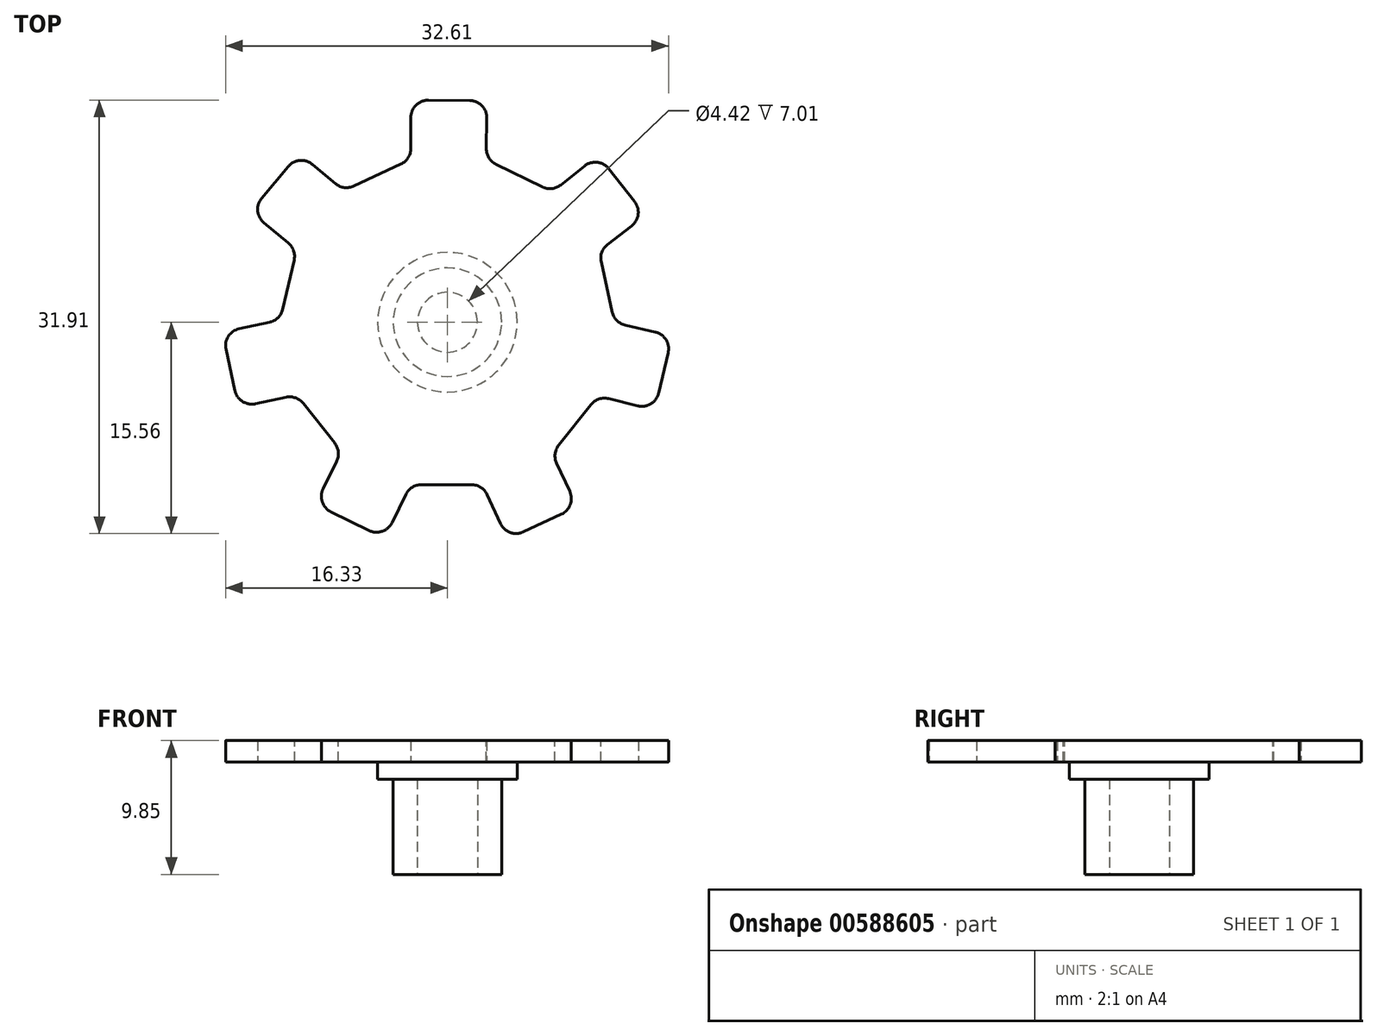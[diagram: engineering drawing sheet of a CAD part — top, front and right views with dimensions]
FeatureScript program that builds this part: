
annotation { "Feature Type Name" : "Feature", "Feature Type Description" : "" }
export const myFeature = defineFeature(function(context is Context, id is Id, definition is map)
    precondition{}
    {
        {
            var Q0;
            Q0=qCreatedBy(makeId("Top.planeOp"),FACE);
            var sketch = newSketch(context, id + "F0", { "sketchPlane" : qUnion([Q0])});
            skLineSegment(sketch, "E0", {"start": v(-2.4, 14.6) * mm, "end": v(-2.4, 10.7) * mm});
            skLineSegment(sketch, "E1", {"start": v(-2.4, 10.7) * mm, "end": v(-6.8, 8.65) * mm});
            skLineSegment(sketch, "E2", {"start": v(-6.8, 8.65) * mm, "end": v(-9.75, 11.1) * mm});
            skLineSegment(sketch, "E3", {"start": v(-9.75, 11.1) * mm, "end": v(-12.94, 7.27) * mm});
            skLineSegment(sketch, "E4", {"start": v(-12.94, 7.27) * mm, "end": v(-9.92, 4.76) * mm});
            skLineSegment(sketch, "E5", {"start": v(-9.92, 4.76) * mm, "end": v(-10.99, 0.15) * mm});
            skLineSegment(sketch, "E6", {"start": v(-10.99, 0.15) * mm, "end": v(-14.79, -0.67) * mm});
            skLineSegment(sketch, "E7", {"start": v(-14.79, -0.67) * mm, "end": v(-13.73, -5.6) * mm});
            skLineSegment(sketch, "E8", {"start": v(-13.73, -5.6) * mm, "end": v(-9.92, -4.78) * mm});
            skLineSegment(sketch, "E9", {"start": v(-9.92, -4.78) * mm, "end": v(-6.97, -8.51) * mm});
            skLineSegment(sketch, "E10", {"start": v(-6.97, -8.51) * mm, "end": v(-8.66, -11.97) * mm});
            skLineSegment(sketch, "E11", {"start": v(-8.66, -11.97) * mm, "end": v(-4.14, -14.2) * mm});
            skLineSegment(sketch, "E12", {"start": v(-4.14, -14.2) * mm, "end": v(-2.42, -10.68) * mm});
            skLineSegment(sketch, "E13", {"start": v(-2.42, -10.68) * mm, "end": v(2.3, -10.68) * mm});
            skLineSegment(sketch, "E14", {"start": v(2.3, -10.68) * mm, "end": v(3.97, -14.26) * mm});
            skLineSegment(sketch, "E15", {"start": v(3.97, -14.26) * mm, "end": v(8.52, -12.15) * mm});
            skLineSegment(sketch, "E16", {"start": v(8.52, -12.15) * mm, "end": v(6.88, -8.63) * mm});
            skLineSegment(sketch, "E17", {"start": v(6.88, -8.63) * mm, "end": v(9.89, -4.84) * mm});
            skLineSegment(sketch, "E18", {"start": v(9.89, -4.84) * mm, "end": v(13.62, -5.78) * mm});
            skLineSegment(sketch, "E19", {"start": v(13.62, -5.78) * mm, "end": v(14.77, -0.9) * mm});
            skLineSegment(sketch, "E20", {"start": v(14.77, -0.9) * mm, "end": v(11, -0.04) * mm});
            skLineSegment(sketch, "E21", {"start": v(11, -0.04) * mm, "end": v(9.95, 4.67) * mm});
            skLineSegment(sketch, "E22", {"start": v(9.95, 4.67) * mm, "end": v(13, 7.03) * mm});
            skLineSegment(sketch, "E23", {"start": v(13, 7.03) * mm, "end": v(9.9, 10.98) * mm});
            skLineSegment(sketch, "E24", {"start": v(9.9, 10.98) * mm, "end": v(6.88, 8.58) * mm});
            skLineSegment(sketch, "E25", {"start": v(6.88, 8.58) * mm, "end": v(2.55, 10.7) * mm});
            skLineSegment(sketch, "E26", {"start": v(2.55, 10.7) * mm, "end": v(2.6, 14.56) * mm});
            skLineSegment(sketch, "E27", {"start": v(2.6, 14.56) * mm, "end": v(-2.4, 14.6) * mm});
            skSolve(sketch);
        }
        {
            var Q0;
            Q0 = qSketchRegion(id + "F0", true);
            extrude(context, id + "F1", {"entities" : qUnion([Q0]), "depth" : 2.54 * mm, "offsetDistance" : 25.4 * mm});
        }
        {
            var Q0;
            Q0=makeQuery(id+"F1.opExtrude","SWEPT_BODY",BODY,{"disambiguationData":[OSD([sQuery(id+"F0.wireOp",EDGE,"E0"),sQuery(id+"F0.wireOp",EDGE,"E1"),sQuery(id+"F0.wireOp",EDGE,"E2"),sQuery(id+"F0.wireOp",EDGE,"E3"),sQuery(id+"F0.wireOp",EDGE,"E4"),sQuery(id+"F0.wireOp",EDGE,"E5"),sQuery(id+"F0.wireOp",EDGE,"E6"),sQuery(id+"F0.wireOp",EDGE,"E7"),sQuery(id+"F0.wireOp",EDGE,"E8"),sQuery(id+"F0.wireOp",EDGE,"E9"),sQuery(id+"F0.wireOp",EDGE,"E10"),sQuery(id+"F0.wireOp",EDGE,"E11"),sQuery(id+"F0.wireOp",EDGE,"E12"),sQuery(id+"F0.wireOp",EDGE,"E13"),sQuery(id+"F0.wireOp",EDGE,"E14"),sQuery(id+"F0.wireOp",EDGE,"E15"),sQuery(id+"F0.wireOp",EDGE,"E16"),sQuery(id+"F0.wireOp",EDGE,"E17"),sQuery(id+"F0.wireOp",EDGE,"E18"),sQuery(id+"F0.wireOp",EDGE,"E19"),sQuery(id+"F0.wireOp",EDGE,"E20"),sQuery(id+"F0.wireOp",EDGE,"E21"),sQuery(id+"F0.wireOp",EDGE,"E22"),sQuery(id+"F0.wireOp",EDGE,"E23"),sQuery(id+"F0.wireOp",EDGE,"E24"),sQuery(id+"F0.wireOp",EDGE,"E25"),sQuery(id+"F0.wireOp",EDGE,"E26"),sQuery(id+"F0.wireOp",EDGE,"E27")])]});
            var Q1;
            Q1=qCreatedBy(makeId("Origin.pointOp"),VERTEX);
            transform(context, id + "F2", {"entities" : qUnion([Q0]), "transformType" : TransformType.SCALE_UNIFORMLY, "scale" : 1.12, "scalePoint" : qUnion([Q1]), "makeCopy" : false});
        }
        {
            var Q0;
            Q0=makeQuery(id+"F1.opExtrude","SWEPT_EDGE",EDGE,{"disambiguationData":[OSD([sQuery(id+"F0.wireOp",EDGE,"E6"),sQuery(id+"F0.wireOp",EDGE,"E7")])]});
            var Q1;
            Q1=makeQuery(id+"F1.opExtrude","SWEPT_EDGE",EDGE,{"disambiguationData":[OSD([sQuery(id+"F0.wireOp",EDGE,"E5"),sQuery(id+"F0.wireOp",EDGE,"E6")])]});
            var Q2;
            {var subQ0=sQuery(id+"F0.wireOp",EDGE,"E4");Q2=makeQuery(id+"Fj5wciNK8VLjmr4_1.opFillet","BLEND_EDGE",EDGE,{"blendedFrom":[makeQuery(id+"F1.opExtrude","CAP_EDGE",EDGE,{"disambiguationData":[OSD([subQ0])],"isStart":false}),makeQuery(id+"F1.opExtrude","SWEPT_FACE",FACE,{"disambiguationData":[OSD([subQ0])]})],"blendedInto":[makeQuery(id+"F1.opExtrude","SWEPT_FACE",FACE,{"disambiguationData":[OSD([subQ0])]})]});}
            var Q3;
            Q3=makeQuery(id+"F1.opExtrude","SWEPT_EDGE",EDGE,{"disambiguationData":[OSD([sQuery(id+"F0.wireOp",EDGE,"E3"),sQuery(id+"F0.wireOp",EDGE,"E4")])]});
            var Q4;
            Q4=makeQuery(id+"F1.opExtrude","SWEPT_EDGE",EDGE,{"disambiguationData":[OSD([sQuery(id+"F0.wireOp",EDGE,"E2"),sQuery(id+"F0.wireOp",EDGE,"E3")])]});
            var Q5;
            Q5=makeQuery(id+"F1.opExtrude","SWEPT_EDGE",EDGE,{"disambiguationData":[OSD([sQuery(id+"F0.wireOp",EDGE,"E1"),sQuery(id+"F0.wireOp",EDGE,"E2")])]});
            var Q6;
            Q6=makeQuery(id+"F1.opExtrude","SWEPT_EDGE",EDGE,{"disambiguationData":[OSD([sQuery(id+"F0.wireOp",EDGE,"E0"),sQuery(id+"F0.wireOp",EDGE,"E1")])]});
            var Q7;
            Q7=makeQuery(id+"F1.opExtrude","SWEPT_EDGE",EDGE,{"disambiguationData":[OSD([sQuery(id+"F0.wireOp",EDGE,"E0"),sQuery(id+"F0.wireOp",EDGE,"E27")])]});
            var Q8;
            Q8=makeQuery(id+"F1.opExtrude","SWEPT_EDGE",EDGE,{"disambiguationData":[OSD([sQuery(id+"F0.wireOp",EDGE,"E26"),sQuery(id+"F0.wireOp",EDGE,"E27")])]});
            var Q9;
            Q9=makeQuery(id+"F1.opExtrude","SWEPT_EDGE",EDGE,{"disambiguationData":[OSD([sQuery(id+"F0.wireOp",EDGE,"E25"),sQuery(id+"F0.wireOp",EDGE,"E26")])]});
            var Q10;
            Q10=makeQuery(id+"F1.opExtrude","SWEPT_EDGE",EDGE,{"disambiguationData":[OSD([sQuery(id+"F0.wireOp",EDGE,"E24"),sQuery(id+"F0.wireOp",EDGE,"E25")])]});
            var Q11;
            Q11=makeQuery(id+"F1.opExtrude","SWEPT_EDGE",EDGE,{"disambiguationData":[OSD([sQuery(id+"F0.wireOp",EDGE,"E23"),sQuery(id+"F0.wireOp",EDGE,"E24")])]});
            var Q12;
            Q12=makeQuery(id+"F1.opExtrude","SWEPT_EDGE",EDGE,{"disambiguationData":[OSD([sQuery(id+"F0.wireOp",EDGE,"E22"),sQuery(id+"F0.wireOp",EDGE,"E23")])]});
            var Q13;
            Q13=makeQuery(id+"F1.opExtrude","SWEPT_EDGE",EDGE,{"disambiguationData":[OSD([sQuery(id+"F0.wireOp",EDGE,"E21"),sQuery(id+"F0.wireOp",EDGE,"E22")])]});
            var Q14;
            Q14=makeQuery(id+"F1.opExtrude","SWEPT_EDGE",EDGE,{"disambiguationData":[OSD([sQuery(id+"F0.wireOp",EDGE,"E20"),sQuery(id+"F0.wireOp",EDGE,"E21")])]});
            var Q15;
            Q15=makeQuery(id+"F1.opExtrude","SWEPT_EDGE",EDGE,{"disambiguationData":[OSD([sQuery(id+"F0.wireOp",EDGE,"E19"),sQuery(id+"F0.wireOp",EDGE,"E20")])]});
            var Q16;
            Q16=makeQuery(id+"F1.opExtrude","SWEPT_EDGE",EDGE,{"disambiguationData":[OSD([sQuery(id+"F0.wireOp",EDGE,"E18"),sQuery(id+"F0.wireOp",EDGE,"E19")])]});
            var Q17;
            Q17=makeQuery(id+"F1.opExtrude","SWEPT_EDGE",EDGE,{"disambiguationData":[OSD([sQuery(id+"F0.wireOp",EDGE,"E17"),sQuery(id+"F0.wireOp",EDGE,"E18")])]});
            var Q18;
            Q18=makeQuery(id+"F1.opExtrude","SWEPT_EDGE",EDGE,{"disambiguationData":[OSD([sQuery(id+"F0.wireOp",EDGE,"E16"),sQuery(id+"F0.wireOp",EDGE,"E17")])]});
            var Q19;
            Q19=makeQuery(id+"F1.opExtrude","SWEPT_EDGE",EDGE,{"disambiguationData":[OSD([sQuery(id+"F0.wireOp",EDGE,"E15"),sQuery(id+"F0.wireOp",EDGE,"E16")])]});
            var Q20;
            Q20=makeQuery(id+"F1.opExtrude","SWEPT_EDGE",EDGE,{"disambiguationData":[OSD([sQuery(id+"F0.wireOp",EDGE,"E14"),sQuery(id+"F0.wireOp",EDGE,"E15")])]});
            var Q21;
            Q21=makeQuery(id+"F1.opExtrude","SWEPT_EDGE",EDGE,{"disambiguationData":[OSD([sQuery(id+"F0.wireOp",EDGE,"E13"),sQuery(id+"F0.wireOp",EDGE,"E14")])]});
            var Q22;
            Q22=makeQuery(id+"F1.opExtrude","SWEPT_EDGE",EDGE,{"disambiguationData":[OSD([sQuery(id+"F0.wireOp",EDGE,"E12"),sQuery(id+"F0.wireOp",EDGE,"E13")])]});
            var Q23;
            Q23=makeQuery(id+"F1.opExtrude","SWEPT_EDGE",EDGE,{"disambiguationData":[OSD([sQuery(id+"F0.wireOp",EDGE,"E11"),sQuery(id+"F0.wireOp",EDGE,"E12")])]});
            var Q24;
            Q24=makeQuery(id+"F1.opExtrude","SWEPT_EDGE",EDGE,{"disambiguationData":[OSD([sQuery(id+"F0.wireOp",EDGE,"E10"),sQuery(id+"F0.wireOp",EDGE,"E11")])]});
            var Q25;
            Q25=makeQuery(id+"F1.opExtrude","SWEPT_EDGE",EDGE,{"disambiguationData":[OSD([sQuery(id+"F0.wireOp",EDGE,"E9"),sQuery(id+"F0.wireOp",EDGE,"E10")])]});
            var Q26;
            Q26=makeQuery(id+"F1.opExtrude","SWEPT_EDGE",EDGE,{"disambiguationData":[OSD([sQuery(id+"F0.wireOp",EDGE,"E8"),sQuery(id+"F0.wireOp",EDGE,"E9")])]});
            var Q27;
            Q27=makeQuery(id+"F1.opExtrude","SWEPT_EDGE",EDGE,{"disambiguationData":[OSD([sQuery(id+"F0.wireOp",EDGE,"E7"),sQuery(id+"F0.wireOp",EDGE,"E8")])]});
            var Q28;
            Q28=makeQuery(id+"F1.opExtrude","SWEPT_EDGE",EDGE,{"disambiguationData":[OSD([sQuery(id+"F0.wireOp",EDGE,"E4"),sQuery(id+"F0.wireOp",EDGE,"E5")])]});
            fillet(context, id + "F3", {"entities" : qUnion([Q0, Q1, Q2, Q3, Q4, Q5, Q6, Q7, Q8, Q9, Q10, Q11, Q12, Q13, Q14, Q15, Q16, Q17, Q18, Q19, Q20, Q21, Q22, Q23, Q24, Q25, Q26, Q27, Q28]), "radius" : 1.27 * mm, "tangentPropagation" : true, "allowEdgeOverflow" : false});
        }
        {
            var Q0;
            Q0=makeQuery(id+"F0.imprint","IMPRINT",FACE,{"disambiguationData":[TD([[makeQuery(id+"F0.imprint","IMPRINT",EDGE,{"derivedFrom":sQuery(id+"F0.wireOp",EDGE,"E0")}),1.0]])]});
            var sketch = newSketch(context, id + "F4", { "sketchPlane" : qUnion([Q0])});
            skCircle(sketch, "E28", {"center": v(0, 0) * mm, "radius": 4 * mm});
            skCircle(sketch, "E29.0", {"center": v(0, 0) * mm, "radius": 2.15 * mm});
            skSolve(sketch);
        }
        {
            var Q0;
            Q0=makeQuery(id+"F4.imprint","IMPRINT",FACE,{"disambiguationData":[TD([[makeQuery(id+"F4.imprint","IMPRINT",EDGE,{"derivedFrom":sQuery(id+"F4.wireOp",EDGE,"E28")}),1.0]])]});
            var Q1;
            Q1=makeQuery(id+"F4.imprint","IMPRINT",FACE,{"disambiguationData":[TD([[makeQuery(id+"F4.imprint","IMPRINT",EDGE,{"derivedFrom":sQuery(id+"F4.wireOp",EDGE,"E29.0")}),1.0]])]});
            extrude(context, id + "F5", {"entities" : qUnion([Q0, Q1]), "operationType" : NewBodyOperationType.ADD, "oppositeDirection" : true, "depth" : 7 * mm, "offsetDistance" : 25.4 * mm});
        }
        {
            var Q0;
            Q0=makeQuery(id+"F5.opExtrude","CAP_FACE",FACE,{"disambiguationData":[OSD([sQuery(id+"F4.wireOp",EDGE,"E28")])],"isStart":false});
            var sketch = newSketch(context, id + "F6", { "sketchPlane" : qUnion([Q0])});
            skCircle(sketch, "E30", {"center": v(0, 0) * mm, "radius": 2.2 * mm});
            skSolve(sketch);
        }
        {
            var Q0;
            Q0=makeQuery(id+"F6.imprint","IMPRINT",FACE,{"disambiguationData":[TD([[makeQuery(id+"F6.imprint","IMPRINT",EDGE,{"derivedFrom":sQuery(id+"F6.wireOp",EDGE,"E30")}),1.0]])]});
            extrude(context, id + "F7", {"entities" : qUnion([Q0]), "operationType" : NewBodyOperationType.REMOVE, "oppositeDirection" : true, "depth" : 7 * mm, "offsetDistance" : 25.4 * mm});
        }
        {
            var Q0;
            Q0=makeQuery(id+"F1.opExtrude","CAP_FACE",FACE,{"disambiguationData":[OSD([sQuery(id+"F0.wireOp",EDGE,"E0"),sQuery(id+"F0.wireOp",EDGE,"E1"),sQuery(id+"F0.wireOp",EDGE,"E2"),sQuery(id+"F0.wireOp",EDGE,"E3"),sQuery(id+"F0.wireOp",EDGE,"E4"),sQuery(id+"F0.wireOp",EDGE,"E5"),sQuery(id+"F0.wireOp",EDGE,"E6"),sQuery(id+"F0.wireOp",EDGE,"E7"),sQuery(id+"F0.wireOp",EDGE,"E8"),sQuery(id+"F0.wireOp",EDGE,"E9"),sQuery(id+"F0.wireOp",EDGE,"E10"),sQuery(id+"F0.wireOp",EDGE,"E11"),sQuery(id+"F0.wireOp",EDGE,"E12"),sQuery(id+"F0.wireOp",EDGE,"E13"),sQuery(id+"F0.wireOp",EDGE,"E14"),sQuery(id+"F0.wireOp",EDGE,"E15"),sQuery(id+"F0.wireOp",EDGE,"E16"),sQuery(id+"F0.wireOp",EDGE,"E17"),sQuery(id+"F0.wireOp",EDGE,"E18"),sQuery(id+"F0.wireOp",EDGE,"E19"),sQuery(id+"F0.wireOp",EDGE,"E20"),sQuery(id+"F0.wireOp",EDGE,"E21"),sQuery(id+"F0.wireOp",EDGE,"E22"),sQuery(id+"F0.wireOp",EDGE,"E23"),sQuery(id+"F0.wireOp",EDGE,"E24"),sQuery(id+"F0.wireOp",EDGE,"E25"),sQuery(id+"F0.wireOp",EDGE,"E26"),sQuery(id+"F0.wireOp",EDGE,"E27")])],"isStart":true});
            extrude(context, id + "F8", {"entities" : qUnion([Q0]), "operationType" : NewBodyOperationType.REMOVE, "oppositeDirection" : true, "depth" : 1.27 * mm, "offsetDistance" : 25.4 * mm});
        }
        {
            var Q0;
            Q0=makeQuery(id+"F0.imprint","IMPRINT",FACE,{"disambiguationData":[TD([[makeQuery(id+"F0.imprint","IMPRINT",EDGE,{"derivedFrom":sQuery(id+"F0.wireOp",EDGE,"E0")}),1.0]])]});
            var sketch = newSketch(context, id + "F9", { "sketchPlane" : qUnion([Q0])});
            skCircle(sketch, "E31", {"center": v(0, 0) * mm, "radius": 5.14 * mm});
            skLineSegment(sketch, "E32", {"start": v(-2.66, 4.4) * mm, "end": v(-2.05, 3.42) * mm, "construction": true});
            skSolve(sketch);
        }
        {
            var Q0;
            Q0 = qSketchRegion(id + "F9", true);
            extrude(context, id + "F10", {"entities" : qUnion([Q0]), "operationType" : NewBodyOperationType.ADD, "depth" : 1.27 * mm, "offsetDistance" : 25.4 * mm});
        }
    });
